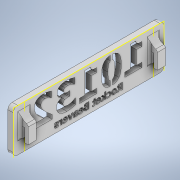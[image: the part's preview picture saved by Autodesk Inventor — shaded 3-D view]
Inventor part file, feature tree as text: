
AUTODESK INVENTOR PART (.ipt)
format: ipt  version: 2020 (Build 240168000, 168)  size: 914,432 bytes
history: native  units: in
note: dims shown in document units (in); Inventor stores cm internally (conversion verified against a paired STEP export)
features: sketch x3, other x2
ambient origin geometry x8: Origin, YZ Plane, XZ Plane, XY Plane, X Axis, Y Axis, Z Axis, Center Point
bodies: Solid1 (feature_tree)
feature tree (5):
  other  "Vehicle Registration Plate Final.iam"
  other  "Vehicle Registration Plate Final.ipt:1"
  sketch  "Sketch6"
  sketch  "Sketch5"
  sketch  "Sketch5_1"  dims[d0=0.3937in]
